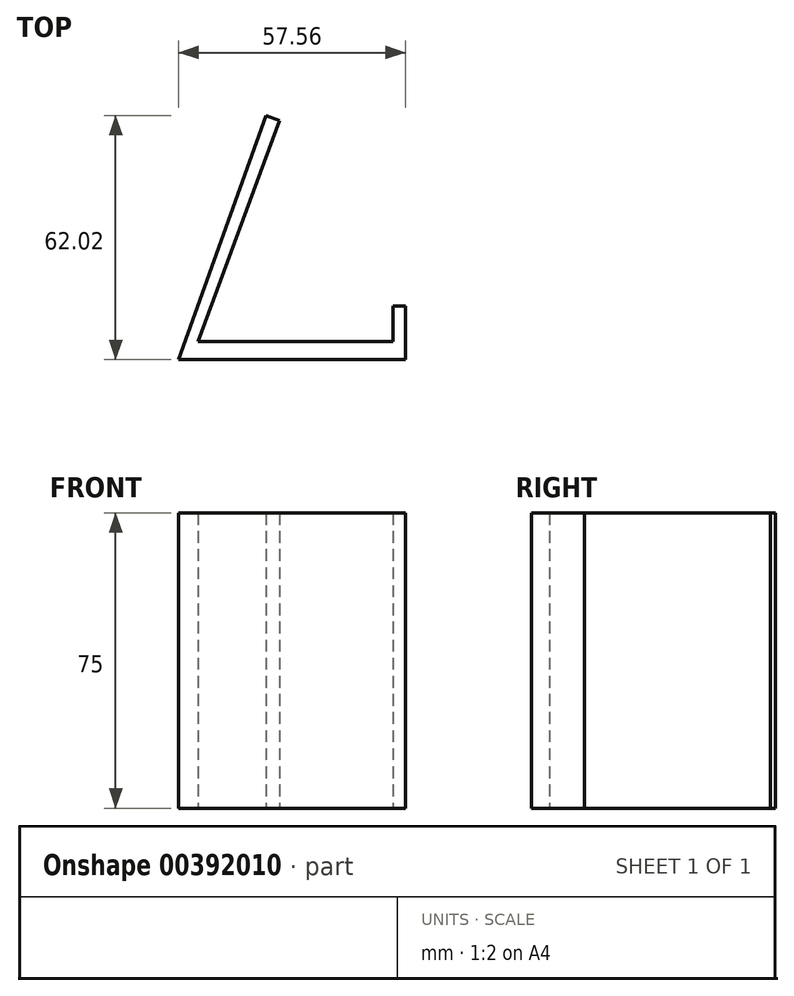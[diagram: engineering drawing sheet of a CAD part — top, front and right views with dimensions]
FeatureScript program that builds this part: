
annotation { "Feature Type Name" : "Feature", "Feature Type Description" : "" }
export const myFeature = defineFeature(function(context is Context, id is Id, definition is map)
    precondition{}
    {
        {
            var Q0;
            Q0=qCreatedBy(makeId("Top.planeOp"),FACE);
            var sketch = newSketch(context, id + "F0", { "sketchPlane" : qUnion([Q0])});
            skLineSegment(sketch, "E0", {"start": v(-31.37, -21) * mm, "end": v(26.2, -21) * mm});
            skLineSegment(sketch, "E1", {"start": v(26.2, -21) * mm, "end": v(26.2, -7.48) * mm});
            skLineSegment(sketch, "E2", {"start": v(26.2, -7.48) * mm, "end": v(23.02, -7.48) * mm});
            skLineSegment(sketch, "E3", {"start": v(23.02, -7.48) * mm, "end": v(23.02, -16.4) * mm});
            skLineSegment(sketch, "E4", {"start": v(23.02, -16.4) * mm, "end": v(-26.48, -16.4) * mm});
            skLineSegment(sketch, "E5", {"start": v(-26.48, -16.4) * mm, "end": v(-5.76, 39.72) * mm});
            skLineSegment(sketch, "E6", {"start": v(-5.76, 39.72) * mm, "end": v(-9.26, 41.01) * mm});
            skLineSegment(sketch, "E7", {"start": v(-9.26, 41.01) * mm, "end": v(-31.37, -21) * mm});
            skSolve(sketch);
        }
        {
            var Q0;
            Q0 = qSketchRegion(id + "F0", true);
            extrude(context, id + "F1", {"entities" : qUnion([Q0]), "depth" : 75 * mm});
        }
    });
